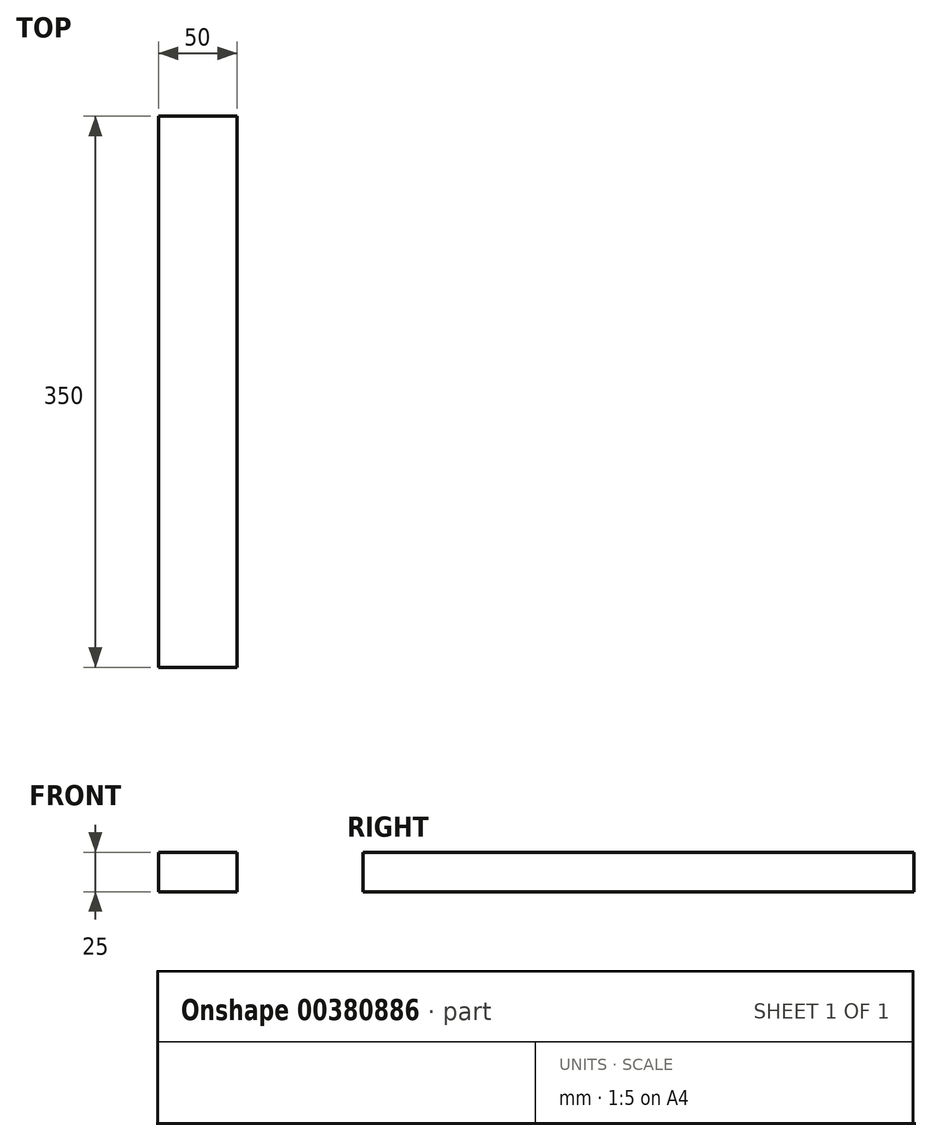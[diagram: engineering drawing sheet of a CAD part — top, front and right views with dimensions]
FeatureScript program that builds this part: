
annotation { "Feature Type Name" : "Feature", "Feature Type Description" : "" }
export const myFeature = defineFeature(function(context is Context, id is Id, definition is map)
    precondition{}
    {
        {
            var Q0;
            Q0=qCreatedBy(makeId("Top.planeOp"),FACE);
            var sketch = newSketch(context, id + "F0", { "sketchPlane" : qUnion([Q0])});
            skLineSegment(sketch, "E0.bottom", {"start": v(-25, 175) * mm, "end": v(25, 175) * mm});
            skLineSegment(sketch, "E0.top", {"start": v(-25, -175) * mm, "end": v(25, -175) * mm});
            skLineSegment(sketch, "E0.left", {"start": v(-25, 175) * mm, "end": v(-25, -175) * mm});
            skLineSegment(sketch, "E0.right", {"start": v(25, 175) * mm, "end": v(25, -175) * mm});
            skPoint(sketch, "E0.middle", {"position": v(0, 0) * mm});
            skSolve(sketch);
        }
        {
            var Q0;
            Q0 = qSketchRegion(id + "F0", true);
            extrude(context, id + "F1", {"entities" : qUnion([Q0]), "depth" : 25 * mm});
        }
    });
